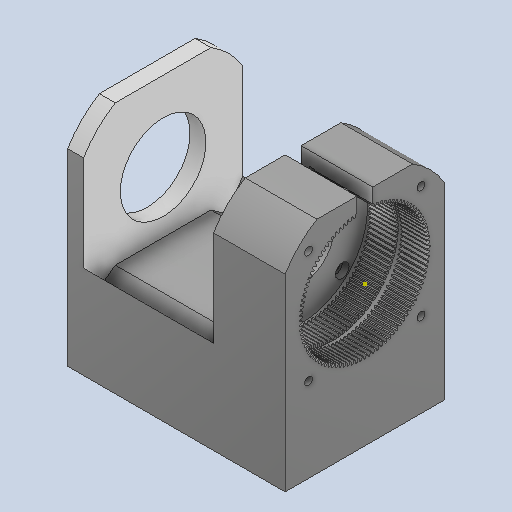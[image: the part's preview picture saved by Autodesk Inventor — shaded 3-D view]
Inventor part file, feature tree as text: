
AUTODESK INVENTOR PART (.ipt)
format: ipt  version: 2022 (Build 260153000, 153)  size: 1,504,768 bytes
history: mixed  units: mm
features: other x3, sketch x3, extrude x2, imported_body x1
ambient origin geometry x8: Origin, YZ Plane, XZ Plane, XY Plane, X Axis, Y Axis, Z Axis, Center Point
bodies: Solid1 (imported_parasolid)
feature tree (9):
  other  "Assembly2.iam"
  other  "96Gears_Stage_1_modified.ipt:1"
  other  "96Gears_Stage_2_modified.ipt:1"
  extrude  "Extrusion3"  Depth=3.0mm
  extrude  "Extrusion5"  Depth=6.0mm TaperAngle=0.0deg
  sketch  "Sketch5"  dims[d7=6.0mm d8=18.0mm d9=0.0mm]
  sketch  "Sketch4"  dims[d0=10.0mm d6=3.0mm]
  sketch  "Sketch7"  dims[d17=32.25mm d18=6.0mm d19=0.0mm]
  imported_body  NMx_Import_Brep_tag  [imported B-rep: ~787 faces, bbox_mm=[82.0, 83.027756, 60.0]]
